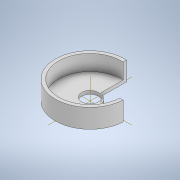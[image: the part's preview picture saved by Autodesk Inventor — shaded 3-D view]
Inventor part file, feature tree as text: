
AUTODESK INVENTOR PART (.ipt)
format: ipt  version: 2022 (Build 260153000, 153)  size: 157,696 bytes
history: native  units: in
note: dims shown in document units (in); Inventor stores cm internally (conversion verified against a paired STEP export)
features: extrude x2, chamfer x1, sketch x1
ambient origin geometry x8: Origin, YZ Plane, XZ Plane, XY Plane, X Axis, Y Axis, Z Axis, Center Point
bodies: Body1 (feature_tree)
feature tree (4):
  extrude  "Extrusion5"  Depth=0.0787in
  chamfer  "Chamfer1"  Distance=0.0394in
  extrude  "Extrusion6"  Depth=0.0787in
  sketch  "Sketch9"  dims[d30=1.6535in d31=0.0394in d32=0.0394in d33=0.0394in d34=0.0394in d35=0.3937in d36=0.0787in d37=0.0in d38=0.4724in d39=0.0197in d40=0.0394in d41=45.0deg d42=0.0787in d43=0.374in d44=0.0in d47=0.0787in d48=0.0787in d49=0.0787in d23=0.5in d24=0.0344in d25=0.5in d26=0.0344in d45=0.0in]
